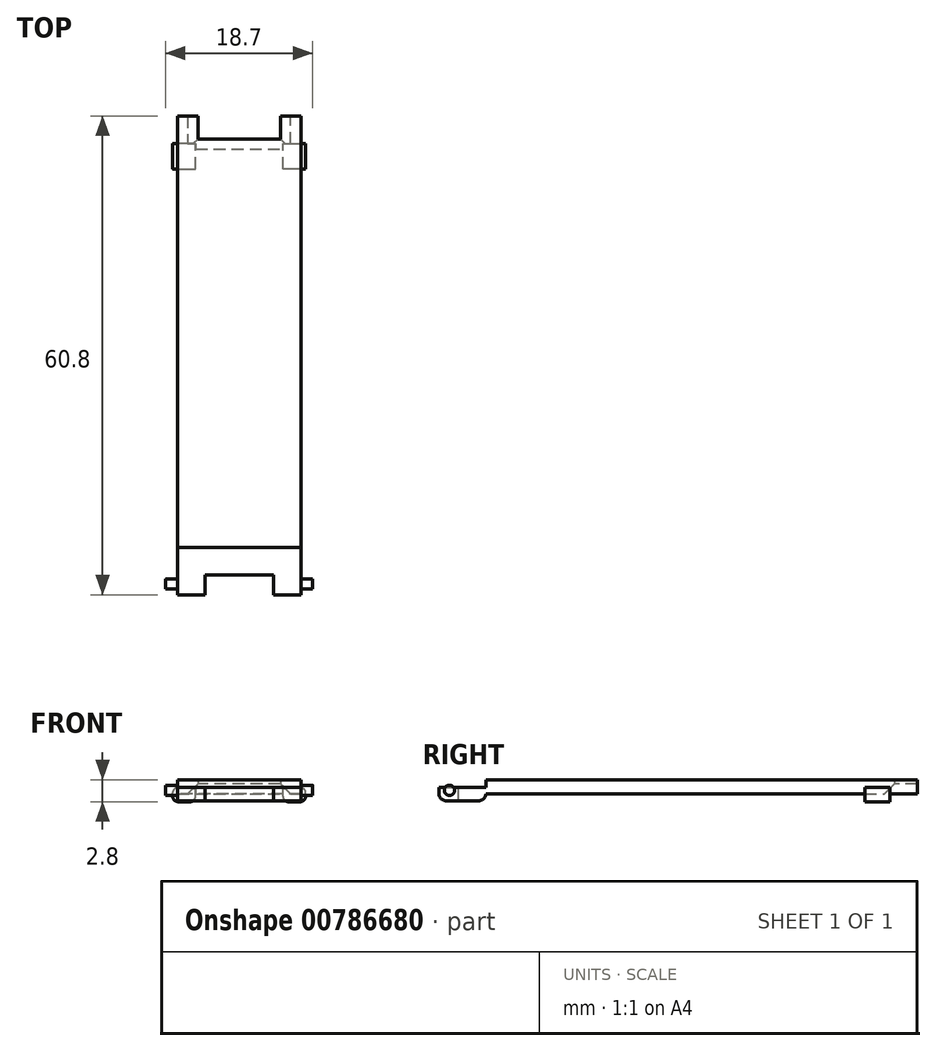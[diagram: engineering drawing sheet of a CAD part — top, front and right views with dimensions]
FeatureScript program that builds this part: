
annotation { "Feature Type Name" : "Feature", "Feature Type Description" : "" }
export const myFeature = defineFeature(function(context is Context, id is Id, definition is map)
    precondition{}
    {
        {
            var Q0;
            Q0=qCreatedBy(makeId("Top.planeOp"),FACE);
            var sketch = newSketch(context, id + "F0", { "sketchPlane" : qUnion([Q0])});
            skLineSegment(sketch, "E0", {"start": v(-6.8, 41.76) * mm, "end": v(-4.2, 41.76) * mm});
            skLineSegment(sketch, "E1", {"start": v(-4.2, 41.76) * mm, "end": v(-4.2, 38.86) * mm});
            skLineSegment(sketch, "E2", {"start": v(-4.2, 38.86) * mm, "end": v(6.3, 38.86) * mm});
            skLineSegment(sketch, "E3", {"start": v(6.3, 38.86) * mm, "end": v(6.3, 41.76) * mm});
            skLineSegment(sketch, "E4", {"start": v(6.3, 41.76) * mm, "end": v(8.9, 41.76) * mm});
            skLineSegment(sketch, "E5", {"start": v(8.9, 41.76) * mm, "end": v(8.9, -19.04) * mm});
            skLineSegment(sketch, "E6", {"start": v(8.9, -19.04) * mm, "end": v(-6.8, -19.04) * mm});
            skLineSegment(sketch, "E7", {"start": v(-6.8, -19.04) * mm, "end": v(-6.8, 41.76) * mm});
            skLineSegment(sketch, "E8", {"start": v(-6.8, 35.06) * mm, "end": v(-7.4, 35.06) * mm});
            skLineSegment(sketch, "E9", {"start": v(-7.4, 35.06) * mm, "end": v(-7.4, 38.26) * mm});
            skLineSegment(sketch, "E10", {"start": v(-7.4, 38.26) * mm, "end": v(-6.8, 38.26) * mm});
            skLineSegment(sketch, "E11", {"start": v(-6.8, 35.06) * mm, "end": v(-4.5, 35.06) * mm});
            skLineSegment(sketch, "E12", {"start": v(-4.5, 35.06) * mm, "end": v(-4.5, 38.26) * mm});
            skLineSegment(sketch, "E13", {"start": v(-4.5, 38.26) * mm, "end": v(-6.8, 38.26) * mm});
            skLineSegment(sketch, "E14", {"start": v(8.9, 35.06) * mm, "end": v(6.6, 35.06) * mm});
            skLineSegment(sketch, "E15", {"start": v(6.6, 35.06) * mm, "end": v(6.6, 38.26) * mm});
            skLineSegment(sketch, "E16", {"start": v(6.6, 38.26) * mm, "end": v(8.9, 38.26) * mm});
            skLineSegment(sketch, "E17", {"start": v(8.9, 38.26) * mm, "end": v(9.5, 38.26) * mm});
            skLineSegment(sketch, "E18", {"start": v(9.5, 38.26) * mm, "end": v(9.5, 35.06) * mm});
            skLineSegment(sketch, "E19", {"start": v(9.5, 35.06) * mm, "end": v(8.9, 35.06) * mm});
            skLineSegment(sketch, "E20", {"start": v(8.9, -19.04) * mm, "end": v(5.4, -19.04) * mm});
            skLineSegment(sketch, "E21", {"start": v(-6.8, -19.04) * mm, "end": v(-3.3, -19.04) * mm});
            skLineSegment(sketch, "E22", {"start": v(-3.3, -19.04) * mm, "end": v(-3.3, -16.54) * mm});
            skLineSegment(sketch, "E23", {"start": v(-3.3, -16.54) * mm, "end": v(5.4, -16.54) * mm});
            skLineSegment(sketch, "E24", {"start": v(5.4, -16.54) * mm, "end": v(5.4, -19.04) * mm});
            skLineSegment(sketch, "E25", {"start": v(8.9, -19.04) * mm, "end": v(8.9, -13.04) * mm});
            skLineSegment(sketch, "E26", {"start": v(8.9, -13.04) * mm, "end": v(-6.8, -13.04) * mm});
            skLineSegment(sketch, "E27", {"start": v(-6.8, -13.04) * mm, "end": v(-6.8, -19.04) * mm});
            skLineSegment(sketch, "E28", {"start": v(8.9, -19.04) * mm, "end": v(8.9, -18.34) * mm});
            skLineSegment(sketch, "E29", {"start": v(8.9, -18.34) * mm, "end": v(10.4, -18.34) * mm});
            skLineSegment(sketch, "E30", {"start": v(10.4, -18.34) * mm, "end": v(10.4, -17.04) * mm});
            skLineSegment(sketch, "E31", {"start": v(10.4, -17.04) * mm, "end": v(8.9, -17.04) * mm});
            skLineSegment(sketch, "E32", {"start": v(-6.8, -19.04) * mm, "end": v(-6.8, -16.04) * mm});
            skLineSegment(sketch, "E33", {"start": v(-6.8, -19.04) * mm, "end": v(-6.8, -18.34) * mm});
            skLineSegment(sketch, "E34", {"start": v(-6.8, -18.34) * mm, "end": v(-8.3, -18.34) * mm});
            skLineSegment(sketch, "E35", {"start": v(-8.3, -18.34) * mm, "end": v(-8.3, -17.04) * mm});
            skLineSegment(sketch, "E36", {"start": v(-8.3, -17.04) * mm, "end": v(-6.8, -17.04) * mm});
            skSolve(sketch);
        }
        {
            var Q0;
            Q0=makeQuery(id+"F0.imprint","IMPRINT",FACE,{"disambiguationData":[TD([[makeQuery(id+"F0.imprint","IMPRINT",EDGE,{"derivedFrom":sQuery(id+"F0.wireOp",EDGE,"E20")}),-1.0]])]});
            var Q1;
            {var subQ7=sQuery(id+"F0.wireOp",EDGE,"E0");Q1=makeQuery(id+"F0.imprint","IMPRINT",FACE,{"disambiguationData":[TD([[makeQuery(id+"F0.imprint","IMPRINT",EDGE,{"derivedFrom":subQ7}),-1.0]])]});}
            var Q2;
            {var subQ0=sQuery(id+"F0.wireOp",EDGE,"E14");Q2=makeQuery(id+"F0.imprint","IMPRINT",FACE,{"disambiguationData":[TD([[makeQuery(id+"F0.imprint","IMPRINT",EDGE,{"derivedFrom":subQ0}),-1.0]])]});}
            var Q3;
            {var subQ0=sQuery(id+"F0.wireOp",EDGE,"E11");Q3=makeQuery(id+"F0.imprint","IMPRINT",FACE,{"disambiguationData":[TD([[makeQuery(id+"F0.imprint","IMPRINT",EDGE,{"derivedFrom":subQ0}),1.0]])]});}
            extrude(context, id + "F1", {"entities" : qUnion([Q0, Q1, Q2, Q3]), "depth" : 1.8 * mm, "offsetDistance" : 25 * mm});
        }
        {
            var Q0;
            Q0=makeQuery(id+"F0.imprint","IMPRINT",FACE,{"disambiguationData":[TD([[makeQuery(id+"F0.imprint","IMPRINT",EDGE,{"derivedFrom":sQuery(id+"F0.wireOp",EDGE,"E6")}),-1.0]])]});
            var Q1;
            Q1=makeQuery(id+"F0.imprint","IMPRINT",FACE,{"disambiguationData":[TD([[makeQuery(id+"F0.imprint","IMPRINT",EDGE,{"derivedFrom":sQuery(id+"F0.wireOp",EDGE,"E20")}),-1.0]])]});
            extrude(context, id + "F2", {"entities" : qUnion([Q0, Q1]), "operationType" : NewBodyOperationType.ADD, "oppositeDirection" : true, "depth" : 0.9 * mm, "offsetDistance" : 25 * mm});
        }
        {
            var Q0;
            {var subQ0=sQuery(id+"F0.wireOp",EDGE,"E14");Q0=makeQuery(id+"F0.imprint","IMPRINT",FACE,{"disambiguationData":[TD([[makeQuery(id+"F0.imprint","IMPRINT",EDGE,{"derivedFrom":subQ0}),-1.0]])]});}
            var Q1;
            {var subQ2=sQuery(id+"F0.wireOp",EDGE,"E17");Q1=makeQuery(id+"F0.imprint","IMPRINT",FACE,{"disambiguationData":[TD([[makeQuery(id+"F0.imprint","IMPRINT",EDGE,{"derivedFrom":subQ2}),-1.0]])]});}
            var Q2;
            {var subQ0=sQuery(id+"F0.wireOp",EDGE,"E11");Q2=makeQuery(id+"F0.imprint","IMPRINT",FACE,{"disambiguationData":[TD([[makeQuery(id+"F0.imprint","IMPRINT",EDGE,{"derivedFrom":subQ0}),1.0]])]});}
            var Q3;
            {var subQ0=sQuery(id+"F0.wireOp",EDGE,"E8");Q3=makeQuery(id+"F0.imprint","IMPRINT",FACE,{"disambiguationData":[TD([[makeQuery(id+"F0.imprint","IMPRINT",EDGE,{"derivedFrom":subQ0}),-1.0]])]});}
            extrude(context, id + "F3", {"entities" : qUnion([Q0, Q1, Q2, Q3]), "operationType" : NewBodyOperationType.ADD, "oppositeDirection" : true, "depth" : 1 * mm, "offsetDistance" : 25 * mm});
        }
        {
            var Q0;
            {var subQ2=sQuery(id+"F0.wireOp",EDGE,"E17");Q0=makeQuery(id+"F0.imprint","IMPRINT",FACE,{"disambiguationData":[TD([[makeQuery(id+"F0.imprint","IMPRINT",EDGE,{"derivedFrom":subQ2}),-1.0]])]});}
            var Q1;
            {var subQ0=sQuery(id+"F0.wireOp",EDGE,"E8");Q1=makeQuery(id+"F0.imprint","IMPRINT",FACE,{"disambiguationData":[TD([[makeQuery(id+"F0.imprint","IMPRINT",EDGE,{"derivedFrom":subQ0}),-1.0]])]});}
            extrude(context, id + "F4", {"entities" : qUnion([Q0, Q1]), "operationType" : NewBodyOperationType.ADD, "depth" : 0.8 * mm, "offsetDistance" : 25 * mm});
        }
        {
            var Q0;
            Q0=makeQuery(id+"F0.imprint","IMPRINT",FACE,{"disambiguationData":[TD([[makeQuery(id+"F0.imprint","IMPRINT",EDGE,{"derivedFrom":sQuery(id+"F0.wireOp",EDGE,"E6")}),-1.0]])]});
            extrude(context, id + "F5", {"entities" : qUnion([Q0]), "operationType" : NewBodyOperationType.ADD, "depth" : 0.8 * mm, "offsetDistance" : 25 * mm});
        }
        {
            var Q0;
            Q0=makeQuery(id+"F1.opExtrude","CAP_EDGE",EDGE,{"disambiguationData":[OSD([sQuery(id+"F0.wireOp",EDGE,"E3")])],"isStart":true});
            var Q1;
            Q1=makeQuery(id+"F1.opExtrude","CAP_EDGE",EDGE,{"disambiguationData":[OSD([sQuery(id+"F0.wireOp",EDGE,"E2")])],"isStart":true});
            var Q2;
            Q2=makeQuery(id+"F1.opExtrude","CAP_EDGE",EDGE,{"disambiguationData":[OSD([sQuery(id+"F0.wireOp",EDGE,"E1")])],"isStart":true});
            chamfer(context, id + "F6", {"entities" : qUnion([Q0, Q1, Q2]), "chamferType" : ChamferType.OFFSET_ANGLE, "width" : 1.3 * mm, "oppositeDirection" : false, "angle" : 45 * degree, "tangentPropagation" : true});
        }
        {
            var Q0;
            Q0=makeQuery(id+"F4.opExtrude","CAP_EDGE",EDGE,{"disambiguationData":[OSD([sQuery(id+"F0.wireOp",EDGE,"E9")])],"isStart":false});
            var Q1;
            Q1=makeQuery(id+"F3.opExtrude","CAP_EDGE",EDGE,{"disambiguationData":[OSD([sQuery(id+"F0.wireOp",EDGE,"E9")])],"isStart":false});
            var Q2;
            Q2=makeQuery(id+"F3.opExtrude","CAP_EDGE",EDGE,{"disambiguationData":[OSD([sQuery(id+"F0.wireOp",EDGE,"E12")])],"isStart":false});
            var Q3;
            Q3=makeQuery(id+"F3.opExtrude","CAP_EDGE",EDGE,{"disambiguationData":[OSD([sQuery(id+"F0.wireOp",EDGE,"E15")])],"isStart":false});
            var Q4;
            Q4=makeQuery(id+"F3.opExtrude","CAP_EDGE",EDGE,{"disambiguationData":[OSD([sQuery(id+"F0.wireOp",EDGE,"E18")])],"isStart":false});
            var Q5;
            Q5=makeQuery(id+"F4.opExtrude","CAP_EDGE",EDGE,{"disambiguationData":[OSD([sQuery(id+"F0.wireOp",EDGE,"E18")])],"isStart":false});
            fillet(context, id + "F7", {"entities" : qUnion([Q0, Q1, Q2, Q3, Q4, Q5]), "radius" : 0.7 * mm, "tangentPropagation" : true, "allowEdgeOverflow" : false});
        }
        {
            var Q0;
            Q0=makeQuery(id+"F1.opExtrude","CAP_EDGE",EDGE,{"disambiguationData":[OSD([sQuery(id+"F0.wireOp",EDGE,"E21")])],"isStart":false});
            var Q1;
            Q1=makeQuery(id+"F2.opExtrude","CAP_EDGE",EDGE,{"disambiguationData":[OSD([sQuery(id+"F0.wireOp",EDGE,"E6"),sQuery(id+"F0.wireOp",EDGE,"E20"),sQuery(id+"F0.wireOp",EDGE,"E21")])],"isStart":false});
            var Q2;
            Q2=makeQuery(id+"F1.opExtrude","CAP_EDGE",EDGE,{"disambiguationData":[OSD([sQuery(id+"F0.wireOp",EDGE,"E20")])],"isStart":false});
            var Q3;
            Q3=makeQuery(id+"F2.opExtrude","CAP_EDGE",EDGE,{"disambiguationData":[OSD([sQuery(id+"F0.wireOp",EDGE,"E26")])],"isStart":false});
            fillet(context, id + "F8", {"entities" : qUnion([Q0, Q1, Q2, Q3]), "radius" : 1 * mm, "tangentPropagation" : true, "allowEdgeOverflow" : false});
        }
        {
            var Q0;
            {var subQ0=sQuery(id+"F0.wireOp",EDGE,"E34");Q0=makeQuery(id+"F0.imprint","IMPRINT",FACE,{"disambiguationData":[TD([[makeQuery(id+"F0.imprint","IMPRINT",EDGE,{"derivedFrom":subQ0}),-1.0]])]});}
            var Q1;
            {var subQ0=sQuery(id+"F0.wireOp",EDGE,"E29");Q1=makeQuery(id+"F0.imprint","IMPRINT",FACE,{"disambiguationData":[TD([[makeQuery(id+"F0.imprint","IMPRINT",EDGE,{"derivedFrom":subQ0}),1.0]])]});}
            extrude(context, id + "F9", {"entities" : qUnion([Q0, Q1]), "operationType" : NewBodyOperationType.ADD, "oppositeDirection" : true, "depth" : 0.2 * mm, "offsetDistance" : 25 * mm});
        }
        {
            var Q0;
            {var subQ0=sQuery(id+"F0.wireOp",EDGE,"E34");Q0=makeQuery(id+"F0.imprint","IMPRINT",FACE,{"disambiguationData":[TD([[makeQuery(id+"F0.imprint","IMPRINT",EDGE,{"derivedFrom":subQ0}),-1.0]])]});}
            var Q1;
            {var subQ0=sQuery(id+"F0.wireOp",EDGE,"E29");Q1=makeQuery(id+"F0.imprint","IMPRINT",FACE,{"disambiguationData":[TD([[makeQuery(id+"F0.imprint","IMPRINT",EDGE,{"derivedFrom":subQ0}),1.0]])]});}
            extrude(context, id + "F10", {"entities" : qUnion([Q0, Q1]), "operationType" : NewBodyOperationType.ADD, "depth" : 1.1 * mm, "offsetDistance" : 25 * mm});
        }
        {
            var Q0;
            Q0=makeQuery(id+"F10.opExtrude","CAP_EDGE",EDGE,{"disambiguationData":[OSD([sQuery(id+"F0.wireOp",EDGE,"E31")])],"isStart":false});
            var Q1;
            Q1=makeQuery(id+"F10.opExtrude","CAP_EDGE",EDGE,{"disambiguationData":[OSD([sQuery(id+"F0.wireOp",EDGE,"E29")])],"isStart":false});
            fillet(context, id + "F11", {"entities" : qUnion([Q0, Q1]), "radius" : 0.65 * mm, "tangentPropagation" : true, "allowEdgeOverflow" : false});
        }
        {
            var Q0;
            Q0=makeQuery(id+"F9.opExtrude","CAP_EDGE",EDGE,{"disambiguationData":[OSD([sQuery(id+"F0.wireOp",EDGE,"E29")])],"isStart":false});
            var Q1;
            Q1=makeQuery(id+"F9.opExtrude","CAP_EDGE",EDGE,{"disambiguationData":[OSD([sQuery(id+"F0.wireOp",EDGE,"E31")])],"isStart":false});
            var Q2;
            Q2=makeQuery(id+"F9.opExtrude","CAP_EDGE",EDGE,{"disambiguationData":[OSD([sQuery(id+"F0.wireOp",EDGE,"E34")])],"isStart":false});
            var Q3;
            Q3=makeQuery(id+"F9.opExtrude","CAP_EDGE",EDGE,{"disambiguationData":[OSD([sQuery(id+"F0.wireOp",EDGE,"E36")])],"isStart":false});
            var Q4;
            Q4=makeQuery(id+"F10.opExtrude","CAP_EDGE",EDGE,{"disambiguationData":[OSD([sQuery(id+"F0.wireOp",EDGE,"E34")])],"isStart":false});
            var Q5;
            Q5=makeQuery(id+"F10.opExtrude","CAP_EDGE",EDGE,{"disambiguationData":[OSD([sQuery(id+"F0.wireOp",EDGE,"E36")])],"isStart":false});
            fillet(context, id + "F12", {"entities" : qUnion([Q0, Q1, Q2, Q3, Q4, Q5]), "radius" : 0.65 * mm, "tangentPropagation" : true, "allowEdgeOverflow" : false});
        }
    });
